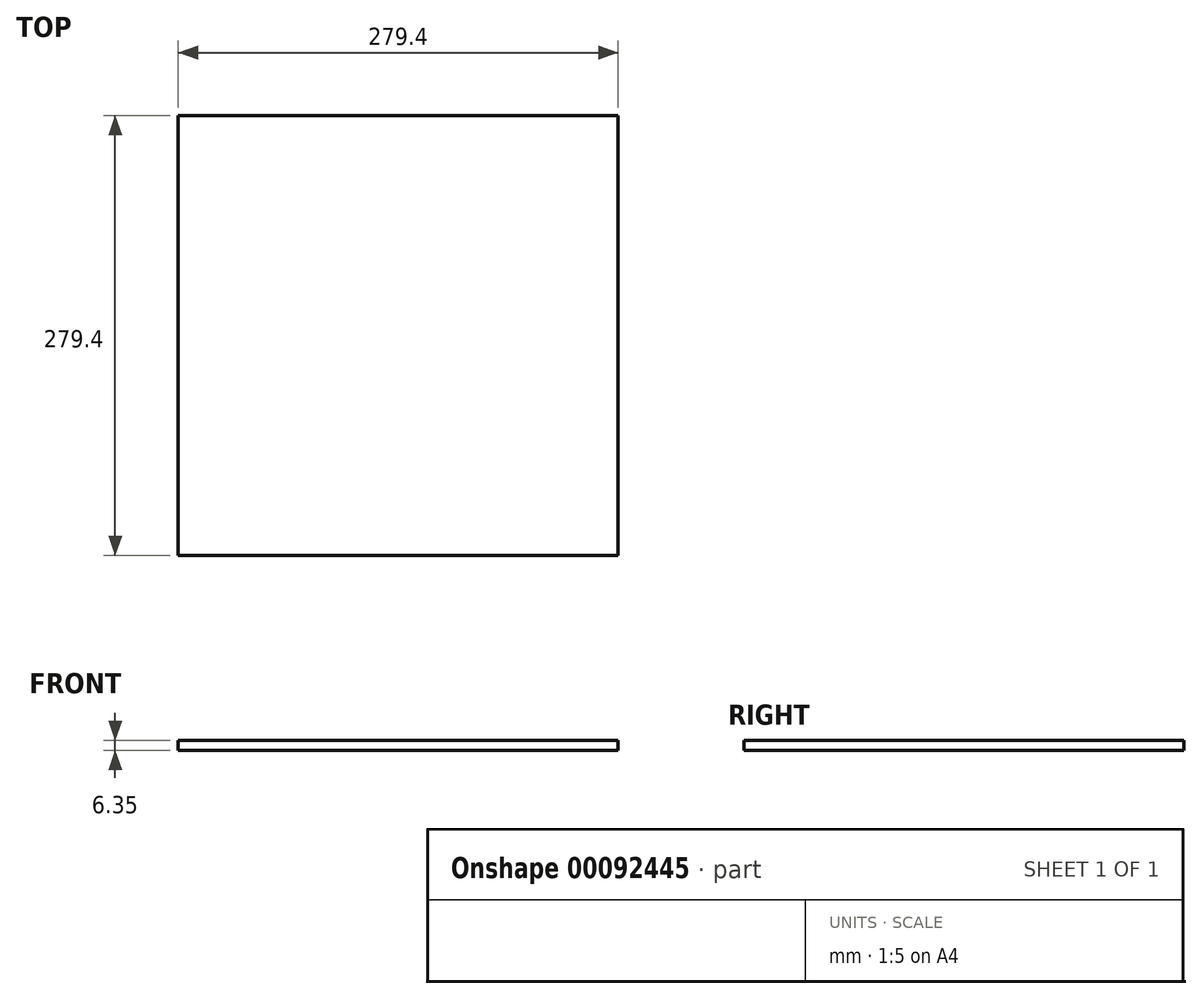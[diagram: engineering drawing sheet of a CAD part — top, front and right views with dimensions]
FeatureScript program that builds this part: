
annotation { "Feature Type Name" : "Feature", "Feature Type Description" : "" }
export const myFeature = defineFeature(function(context is Context, id is Id, definition is map)
    precondition{}
    {
        {
            var Q0;
            Q0=qCreatedBy(makeId("Front.planeOp"),FACE);
            var sketch = newSketch(context, id + "F0", { "sketchPlane" : qUnion([Q0])});
            skLineSegment(sketch, "E0.bottom", {"start": v(235, 6.35) * mm, "end": v(-44.4, 6.35) * mm});
            skLineSegment(sketch, "E0.top", {"start": v(235, 0) * mm, "end": v(-44.4, 0) * mm});
            skLineSegment(sketch, "E0.left", {"start": v(235, 6.35) * mm, "end": v(235, 0) * mm});
            skLineSegment(sketch, "E0.right", {"start": v(-44.4, 6.35) * mm, "end": v(-44.4, 0) * mm});
            skSolve(sketch);
        }
        {
            var Q0;
            Q0=makeQuery(id+"F0.imprint","IMPRINT",FACE,{"disambiguationData":[TD([[makeQuery(id+"F0.imprint","IMPRINT",EDGE,{"derivedFrom":sQuery(id+"F0.wireOp",EDGE,"E0.bottom")}),1.0]])]});
            extrude(context, id + "F1", {"entities" : qUnion([Q0]), "depth" : 279.4 * mm});
        }
    });
